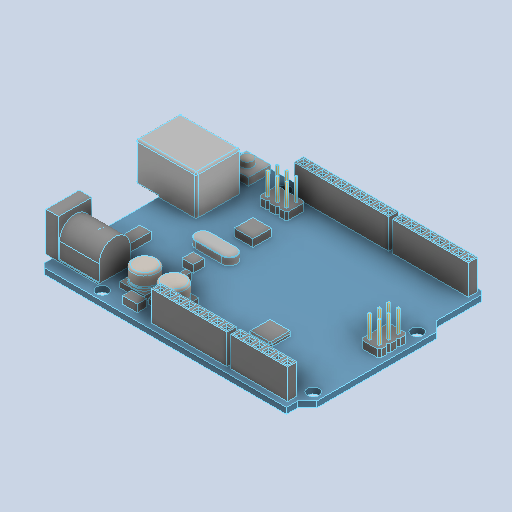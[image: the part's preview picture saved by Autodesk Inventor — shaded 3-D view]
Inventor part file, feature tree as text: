
AUTODESK INVENTOR PART (.ipt)
format: ipt  version: 2024 (Build 280153000, 153)  size: 493,056 bytes
history: native  units: in
note: dims shown in document units (in); Inventor stores cm internally (conversion verified against a paired STEP export)
features: other x1, fillet x1
ambient origin geometry x8: Origin, YZ Plane, XZ Plane, XY Plane, X Axis, Y Axis, Z Axis, Center Point
bodies: Solid1 (feature_tree)
feature tree (2):
  other  "Decoupe"
  fillet  "Congé3"  [1 undecoded]
note: 1 required parameter value undecoded (feature->parameter linkage not recoverable at this tier; creation-order binding heuristic only, values carry confidence <= 0.55)
